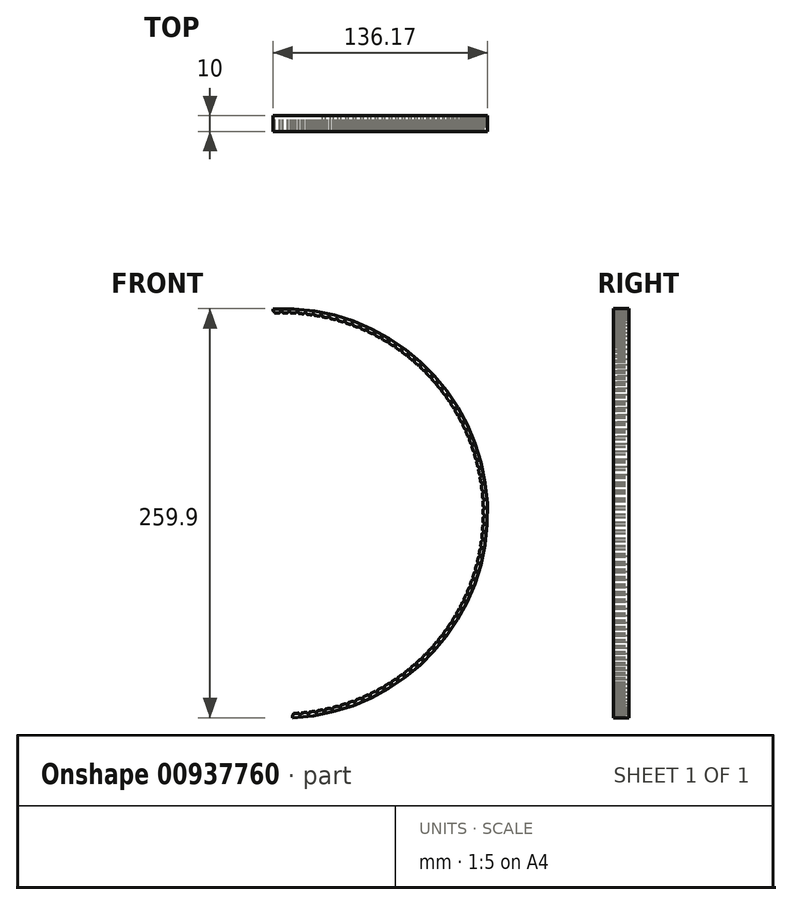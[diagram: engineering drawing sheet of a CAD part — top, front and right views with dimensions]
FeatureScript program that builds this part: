
annotation { "Feature Type Name" : "Feature", "Feature Type Description" : "" }
export const myFeature = defineFeature(function(context is Context, id is Id, definition is map)
    precondition{}
    {
        {
            var Q0;
            Q0=qCreatedBy(makeId("Front.planeOp"),FACE);
            var sketch = newSketch(context, id + "F0", { "sketchPlane" : qUnion([Q0])});
            skArc(sketch, "E0", {"start": v(-165.86, 72.13) * mm, "mid": v(-167.22, 72.1) * mm, "end": v(-168.6, 72.05) * mm});
            skArc(sketch, "E1", {"start": v(-157.54, -185.05) * mm, "mid": v(-33.83, -49.02) * mm, "end": v(-169.86, 74.7) * mm});
            skEllipticalArc(sketch, "E2.5.0.0", {});
            skArc(sketch, "E2.5.0.1", {"start": v(-169.02, 72.47) * mm, "mid": v(-168.84, 72.2) * mm, "end": v(-168.57, 72.04) * mm});
            skEllipticalArc(sketch, "E2.5.0.3", {});
            skEllipticalArc(sketch, "E3.1.0", {});
            skArc(sketch, "E3.1.1", {"start": v(-163.94, 72.58) * mm, "mid": v(-163.77, 72.31) * mm, "end": v(-163.5, 72.14) * mm});
            skEllipticalArc(sketch, "E3.2.0", {});
            skArc(sketch, "E3.2.1", {"start": v(-158.86, 72.49) * mm, "mid": v(-158.7, 72.21) * mm, "end": v(-158.45, 72.03) * mm});
            skEllipticalArc(sketch, "E3.3.0", {});
            skArc(sketch, "E3.3.1", {"start": v(-153.79, 72.2) * mm, "mid": v(-153.64, 71.91) * mm, "end": v(-153.4, 71.72) * mm});
            skEllipticalArc(sketch, "E3.4.0", {});
            skArc(sketch, "E3.4.1", {"start": v(-148.73, 71.7) * mm, "mid": v(-148.6, 71.41) * mm, "end": v(-148.36, 71.2) * mm});
            skEllipticalArc(sketch, "E3.5.0", {});
            skArc(sketch, "E3.5.1", {"start": v(-143.7, 71) * mm, "mid": v(-143.57, 70.71) * mm, "end": v(-143.34, 70.5) * mm});
            skEllipticalArc(sketch, "E3.6.0", {});
            skArc(sketch, "E3.6.1", {"start": v(-138.7, 70.1) * mm, "mid": v(-138.59, 69.81) * mm, "end": v(-138.36, 69.59) * mm});
            skEllipticalArc(sketch, "E3.7.0", {});
            skArc(sketch, "E3.7.1", {"start": v(-133.74, 69.01) * mm, "mid": v(-133.64, 68.71) * mm, "end": v(-133.42, 68.48) * mm});
            skEllipticalArc(sketch, "E3.8.0", {});
            skArc(sketch, "E3.8.1", {"start": v(-128.82, 67.72) * mm, "mid": v(-128.73, 67.42) * mm, "end": v(-128.53, 67.18) * mm});
            skEllipticalArc(sketch, "E3.9.0", {});
            skArc(sketch, "E3.9.1", {"start": v(-123.96, 66.24) * mm, "mid": v(-123.89, 65.93) * mm, "end": v(-123.7, 65.68) * mm});
            skEllipticalArc(sketch, "E3.10.0", {});
            skArc(sketch, "E3.10.1", {"start": v(-119.17, 64.56) * mm, "mid": v(-119.1, 64.25) * mm, "end": v(-118.92, 64) * mm});
            skEllipticalArc(sketch, "E3.11.0", {});
            skArc(sketch, "E3.11.1", {"start": v(-114.44, 62.7) * mm, "mid": v(-114.4, 62.39) * mm, "end": v(-114.22, 62.12) * mm});
            skEllipticalArc(sketch, "E3.12.0", {});
            skArc(sketch, "E3.12.1", {"start": v(-109.8, 60.64) * mm, "mid": v(-109.76, 60.33) * mm, "end": v(-109.6, 60.06) * mm});
            skEllipticalArc(sketch, "E3.13.0", {});
            skArc(sketch, "E3.13.1", {"start": v(-105.23, 58.4) * mm, "mid": v(-105.2, 58.1) * mm, "end": v(-105.06, 57.82) * mm});
            skEllipticalArc(sketch, "E3.14.0", {});
            skArc(sketch, "E3.14.1", {"start": v(-100.76, 56) * mm, "mid": v(-100.75, 55.68) * mm, "end": v(-100.6, 55.4) * mm});
            skEllipticalArc(sketch, "E3.15.0", {});
            skArc(sketch, "E3.15.1", {"start": v(-96.4, 53.4) * mm, "mid": v(-96.4, 53.09) * mm, "end": v(-96.26, 52.8) * mm});
            skEllipticalArc(sketch, "E3.16.0", {});
            skArc(sketch, "E3.16.1", {"start": v(-92.13, 50.64) * mm, "mid": v(-92.14, 50.33) * mm, "end": v(-92.02, 50.04) * mm});
            skEllipticalArc(sketch, "E3.17.0", {});
            skArc(sketch, "E3.17.1", {"start": v(-87.98, 47.71) * mm, "mid": v(-88, 47.4) * mm, "end": v(-87.9, 47.1) * mm});
            skEllipticalArc(sketch, "E3.18.0", {});
            skArc(sketch, "E3.18.1", {"start": v(-83.95, 44.62) * mm, "mid": v(-83.99, 44.3) * mm, "end": v(-83.9, 44) * mm});
            skEllipticalArc(sketch, "E3.19.0", {});
            skArc(sketch, "E3.19.1", {"start": v(-80.04, 41.37) * mm, "mid": v(-80.1, 41.06) * mm, "end": v(-80.01, 40.76) * mm});
            skEllipticalArc(sketch, "E3.20.0", {});
            skArc(sketch, "E3.20.1", {"start": v(-76.27, 37.97) * mm, "mid": v(-76.33, 37.66) * mm, "end": v(-76.26, 37.35) * mm});
            skEllipticalArc(sketch, "E3.21.0", {});
            skArc(sketch, "E3.21.1", {"start": v(-72.64, 34.42) * mm, "mid": v(-72.71, 34.11) * mm, "end": v(-72.65, 33.8) * mm});
            skEllipticalArc(sketch, "E3.22.0", {});
            skArc(sketch, "E3.22.1", {"start": v(-69.15, 30.73) * mm, "mid": v(-69.23, 30.42) * mm, "end": v(-69.19, 30.11) * mm});
            skEllipticalArc(sketch, "E3.23.0", {});
            skArc(sketch, "E3.23.1", {"start": v(-65.8, 26.9) * mm, "mid": v(-65.9, 26.6) * mm, "end": v(-65.87, 26.29) * mm});
            skEllipticalArc(sketch, "E3.24.0", {});
            skArc(sketch, "E3.24.1", {"start": v(-62.62, 22.94) * mm, "mid": v(-62.73, 22.65) * mm, "end": v(-62.71, 22.33) * mm});
            skEllipticalArc(sketch, "E3.25.0", {});
            skArc(sketch, "E3.25.1", {"start": v(-59.6, 18.86) * mm, "mid": v(-59.72, 18.57) * mm, "end": v(-59.7, 18.25) * mm});
            skEllipticalArc(sketch, "E3.26.0", {});
            skArc(sketch, "E3.26.1", {"start": v(-56.73, 14.66) * mm, "mid": v(-56.87, 14.38) * mm, "end": v(-56.87, 14.06) * mm});
            skEllipticalArc(sketch, "E3.27.0", {});
            skArc(sketch, "E3.27.1", {"start": v(-54.04, 10.35) * mm, "mid": v(-54.19, 10.07) * mm, "end": v(-54.2, 9.76) * mm});
            skEllipticalArc(sketch, "E3.28.0", {});
            skArc(sketch, "E3.28.1", {"start": v(-51.52, 5.94) * mm, "mid": v(-51.68, 5.67) * mm, "end": v(-51.7, 5.35) * mm});
            skEllipticalArc(sketch, "E3.29.0", {});
            skArc(sketch, "E3.29.1", {"start": v(-49.18, 1.43) * mm, "mid": v(-49.35, 1.17) * mm, "end": v(-49.4, 0.85) * mm});
            skEllipticalArc(sketch, "E3.30.0", {});
            skArc(sketch, "E3.30.1", {"start": v(-47.02, -3.16) * mm, "mid": v(-47.2, -3.42) * mm, "end": v(-47.25, -3.74) * mm});
            skEllipticalArc(sketch, "E3.31.0", {});
            skArc(sketch, "E3.31.1", {"start": v(-45.05, -7.84) * mm, "mid": v(-45.23, -8.1) * mm, "end": v(-45.3, -8.4) * mm});
            skEllipticalArc(sketch, "E3.32.0", {});
            skArc(sketch, "E3.32.1", {"start": v(-43.26, -12.6) * mm, "mid": v(-43.46, -12.85) * mm, "end": v(-43.53, -13.15) * mm});
            skEllipticalArc(sketch, "E3.33.0", {});
            skArc(sketch, "E3.33.1", {"start": v(-41.66, -17.42) * mm, "mid": v(-41.87, -17.66) * mm, "end": v(-41.96, -17.96) * mm});
            skEllipticalArc(sketch, "E3.34.0", {});
            skArc(sketch, "E3.34.1", {"start": v(-40.26, -22.3) * mm, "mid": v(-40.47, -22.53) * mm, "end": v(-40.58, -22.83) * mm});
            skEllipticalArc(sketch, "E3.35.0", {});
            skArc(sketch, "E3.35.1", {"start": v(-39.05, -27.24) * mm, "mid": v(-39.27, -27.46) * mm, "end": v(-39.39, -27.75) * mm});
            skEllipticalArc(sketch, "E3.36.0", {});
            skArc(sketch, "E3.36.1", {"start": v(-38.04, -32.22) * mm, "mid": v(-38.27, -32.43) * mm, "end": v(-38.4, -32.72) * mm});
            skEllipticalArc(sketch, "E3.37.0", {});
            skArc(sketch, "E3.37.1", {"start": v(-37.22, -37.23) * mm, "mid": v(-37.46, -37.43) * mm, "end": v(-37.6, -37.72) * mm});
            skEllipticalArc(sketch, "E3.38.0", {});
            skArc(sketch, "E3.38.1", {"start": v(-36.6, -42.27) * mm, "mid": v(-36.86, -42.47) * mm, "end": v(-37, -42.74) * mm});
            skEllipticalArc(sketch, "E3.39.0", {});
            skArc(sketch, "E3.39.1", {"start": v(-36.2, -47.34) * mm, "mid": v(-36.45, -47.52) * mm, "end": v(-36.61, -47.8) * mm});
            skEllipticalArc(sketch, "E3.40.0", {});
            skArc(sketch, "E3.40.1", {"start": v(-35.99, -52.41) * mm, "mid": v(-36.25, -52.59) * mm, "end": v(-36.42, -52.85) * mm});
            skEllipticalArc(sketch, "E3.41.0", {});
            skArc(sketch, "E3.41.1", {"start": v(-35.98, -57.5) * mm, "mid": v(-36.25, -57.65) * mm, "end": v(-36.43, -57.91) * mm});
            skEllipticalArc(sketch, "E3.42.0", {});
            skArc(sketch, "E3.42.1", {"start": v(-36.17, -62.57) * mm, "mid": v(-36.45, -62.72) * mm, "end": v(-36.64, -62.97) * mm});
            skEllipticalArc(sketch, "E3.43.0", {});
            skArc(sketch, "E3.43.1", {"start": v(-36.56, -67.63) * mm, "mid": v(-36.85, -67.77) * mm, "end": v(-37.05, -68.02) * mm});
            skEllipticalArc(sketch, "E3.44.0", {});
            skArc(sketch, "E3.44.1", {"start": v(-37.16, -72.68) * mm, "mid": v(-37.45, -72.8) * mm, "end": v(-37.66, -73.04) * mm});
            skEllipticalArc(sketch, "E3.45.0", {});
            skArc(sketch, "E3.45.1", {"start": v(-37.96, -77.7) * mm, "mid": v(-38.25, -77.81) * mm, "end": v(-38.47, -78.04) * mm});
            skEllipticalArc(sketch, "E3.46.0", {});
            skArc(sketch, "E3.46.1", {"start": v(-38.95, -82.68) * mm, "mid": v(-39.25, -82.78) * mm, "end": v(-39.48, -83) * mm});
            skEllipticalArc(sketch, "E3.47.0", {});
            skArc(sketch, "E3.47.1", {"start": v(-40.14, -87.62) * mm, "mid": v(-40.44, -87.71) * mm, "end": v(-40.68, -87.92) * mm});
            skEllipticalArc(sketch, "E3.48.0", {});
            skArc(sketch, "E3.48.1", {"start": v(-41.53, -92.5) * mm, "mid": v(-41.83, -92.59) * mm, "end": v(-42.08, -92.78) * mm});
            skEllipticalArc(sketch, "E3.49.0", {});
            skArc(sketch, "E3.49.1", {"start": v(-43.11, -97.33) * mm, "mid": v(-43.42, -97.4) * mm, "end": v(-43.67, -97.6) * mm});
            skEllipticalArc(sketch, "E3.50.0", {});
            skArc(sketch, "E3.50.1", {"start": v(-44.88, -102.1) * mm, "mid": v(-45.2, -102.15) * mm, "end": v(-45.45, -102.33) * mm});
            skEllipticalArc(sketch, "E3.51.0", {});
            skArc(sketch, "E3.51.1", {"start": v(-46.84, -106.78) * mm, "mid": v(-47.15, -106.83) * mm, "end": v(-47.42, -107) * mm});
            skEllipticalArc(sketch, "E3.52.0", {});
            skArc(sketch, "E3.52.1", {"start": v(-48.99, -111.39) * mm, "mid": v(-49.3, -111.42) * mm, "end": v(-49.57, -111.58) * mm});
            skEllipticalArc(sketch, "E3.53.0", {});
            skArc(sketch, "E3.53.1", {"start": v(-51.31, -115.9) * mm, "mid": v(-51.63, -115.92) * mm, "end": v(-51.9, -116.07) * mm});
            skEllipticalArc(sketch, "E3.54.0", {});
            skArc(sketch, "E3.54.1", {"start": v(-53.81, -120.32) * mm, "mid": v(-54.13, -120.33) * mm, "end": v(-54.41, -120.47) * mm});
            skEllipticalArc(sketch, "E3.55.0", {});
            skArc(sketch, "E3.55.1", {"start": v(-56.5, -124.64) * mm, "mid": v(-56.8, -124.64) * mm, "end": v(-57.1, -124.76) * mm});
            skEllipticalArc(sketch, "E3.56.0", {});
            skArc(sketch, "E3.56.1", {"start": v(-59.34, -128.85) * mm, "mid": v(-59.65, -128.83) * mm, "end": v(-59.95, -128.94) * mm});
            skEllipticalArc(sketch, "E3.57.0", {});
            skArc(sketch, "E3.57.1", {"start": v(-62.35, -132.94) * mm, "mid": v(-62.66, -132.91) * mm, "end": v(-62.96, -133.01) * mm});
            skEllipticalArc(sketch, "E3.58.0", {});
            skArc(sketch, "E3.58.1", {"start": v(-65.52, -136.9) * mm, "mid": v(-65.83, -136.87) * mm, "end": v(-66.13, -136.95) * mm});
            skEllipticalArc(sketch, "E3.59.0", {});
            skArc(sketch, "E3.59.1", {"start": v(-68.85, -140.75) * mm, "mid": v(-69.16, -140.7) * mm, "end": v(-69.46, -140.77) * mm});
            skEllipticalArc(sketch, "E3.60.0", {});
            skArc(sketch, "E3.60.1", {"start": v(-72.32, -144.45) * mm, "mid": v(-72.63, -144.38) * mm, "end": v(-72.94, -144.45) * mm});
            skEllipticalArc(sketch, "E3.61.0", {});
            skArc(sketch, "E3.61.1", {"start": v(-75.95, -148.02) * mm, "mid": v(-76.25, -147.94) * mm, "end": v(-76.56, -147.99) * mm});
            skEllipticalArc(sketch, "E3.62.0", {});
            skArc(sketch, "E3.62.1", {"start": v(-79.7, -151.43) * mm, "mid": v(-80, -151.34) * mm, "end": v(-80.32, -151.38) * mm});
            skEllipticalArc(sketch, "E3.63.0", {});
            skArc(sketch, "E3.63.1", {"start": v(-83.6, -154.7) * mm, "mid": v(-83.9, -154.6) * mm, "end": v(-84.21, -154.62) * mm});
            skEllipticalArc(sketch, "E3.64.0", {});
            skArc(sketch, "E3.64.1", {"start": v(-87.62, -157.8) * mm, "mid": v(-87.91, -157.69) * mm, "end": v(-88.23, -157.7) * mm});
            skEllipticalArc(sketch, "E3.65.0", {});
            skArc(sketch, "E3.65.1", {"start": v(-91.76, -160.75) * mm, "mid": v(-92.05, -160.62) * mm, "end": v(-92.36, -160.62) * mm});
            skEllipticalArc(sketch, "E3.66.0", {});
            skArc(sketch, "E3.66.1", {"start": v(-96.01, -163.52) * mm, "mid": v(-96.3, -163.38) * mm, "end": v(-96.61, -163.37) * mm});
            skEllipticalArc(sketch, "E3.67.0", {});
            skArc(sketch, "E3.67.1", {"start": v(-100.37, -166.13) * mm, "mid": v(-100.65, -165.98) * mm, "end": v(-100.97, -165.96) * mm});
            skEllipticalArc(sketch, "E3.68.0", {});
            skArc(sketch, "E3.68.1", {"start": v(-104.84, -168.56) * mm, "mid": v(-105.1, -168.4) * mm, "end": v(-105.42, -168.36) * mm});
            skEllipticalArc(sketch, "E3.69.0", {});
            skArc(sketch, "E3.69.1", {"start": v(-109.39, -170.8) * mm, "mid": v(-109.65, -170.64) * mm, "end": v(-109.96, -170.6) * mm});
            skEllipticalArc(sketch, "E3.70.0", {});
            skArc(sketch, "E3.70.1", {"start": v(-114.03, -172.88) * mm, "mid": v(-114.29, -172.7) * mm, "end": v(-114.6, -172.64) * mm});
            skEllipticalArc(sketch, "E3.71.0", {});
            skArc(sketch, "E3.71.1", {"start": v(-118.75, -174.76) * mm, "mid": v(-119, -174.57) * mm, "end": v(-119.3, -174.5) * mm});
            skEllipticalArc(sketch, "E3.72.0", {});
            skArc(sketch, "E3.72.1", {"start": v(-123.54, -176.45) * mm, "mid": v(-123.78, -176.25) * mm, "end": v(-124.08, -176.17) * mm});
            skEllipticalArc(sketch, "E3.73.0", {});
            skArc(sketch, "E3.73.1", {"start": v(-128.4, -177.95) * mm, "mid": v(-128.62, -177.74) * mm, "end": v(-128.92, -177.65) * mm});
            skEllipticalArc(sketch, "E3.74.0", {});
            skArc(sketch, "E3.74.1", {"start": v(-133.3, -179.26) * mm, "mid": v(-133.53, -179.04) * mm, "end": v(-133.82, -178.93) * mm});
            skEllipticalArc(sketch, "E3.75.0", {});
            skArc(sketch, "E3.75.1", {"start": v(-138.26, -180.37) * mm, "mid": v(-138.47, -180.14) * mm, "end": v(-138.76, -180.02) * mm});
            skEllipticalArc(sketch, "E3.76.0", {});
            skArc(sketch, "E3.76.1", {"start": v(-143.25, -181.29) * mm, "mid": v(-143.46, -181.05) * mm, "end": v(-143.75, -180.92) * mm});
            skEllipticalArc(sketch, "E3.77.0", {});
            skArc(sketch, "E3.77.1", {"start": v(-148.28, -182) * mm, "mid": v(-148.48, -181.75) * mm, "end": v(-148.76, -181.61) * mm});
            skEllipticalArc(sketch, "E3.78.0", {});
            skArc(sketch, "E3.78.1", {"start": v(-153.34, -182.51) * mm, "mid": v(-153.53, -182.26) * mm, "end": v(-153.8, -182.1) * mm});
            skLineSegment(sketch, "E3.anchor1", {"start": v(-163.71, -55.18) * mm, "end": v(-169.73, 72.2) * mm, "construction": true});
            skLineSegment(sketch, "E3.anchor2", {"start": v(-163.71, -55.18) * mm, "end": v(-157.7, -182.55) * mm, "construction": true});
            skArc(sketch, "E4.1.0", {"start": v(-165.86, 72.13) * mm, "mid": v(-165.56, 72.3) * mm, "end": v(-165.36, 72.57) * mm});
            skEllipticalArc(sketch, "E4.1.1", {});
            skArc(sketch, "E4.2.0", {"start": v(-160.8, 72.11) * mm, "mid": v(-160.49, 72.27) * mm, "end": v(-160.28, 72.54) * mm});
            skEllipticalArc(sketch, "E4.2.1", {});
            skArc(sketch, "E4.3.0", {"start": v(-155.74, 71.9) * mm, "mid": v(-155.42, 72.04) * mm, "end": v(-155.2, 72.3) * mm});
            skEllipticalArc(sketch, "E4.3.1", {});
            skArc(sketch, "E4.4.0", {"start": v(-150.69, 71.48) * mm, "mid": v(-150.37, 71.6) * mm, "end": v(-150.15, 71.86) * mm});
            skEllipticalArc(sketch, "E4.4.1", {});
            skArc(sketch, "E4.5.0", {"start": v(-145.66, 70.86) * mm, "mid": v(-145.34, 70.98) * mm, "end": v(-145.1, 71.22) * mm});
            skEllipticalArc(sketch, "E4.5.1", {});
            skArc(sketch, "E4.6.0", {"start": v(-140.67, 70.04) * mm, "mid": v(-140.34, 70.15) * mm, "end": v(-140.1, 70.38) * mm});
            skEllipticalArc(sketch, "E4.6.1", {});
            skArc(sketch, "E4.7.0", {"start": v(-135.7, 69.03) * mm, "mid": v(-135.38, 69.12) * mm, "end": v(-135.12, 69.34) * mm});
            skEllipticalArc(sketch, "E4.7.1", {});
            skArc(sketch, "E4.8.0", {"start": v(-130.8, 67.82) * mm, "mid": v(-130.46, 67.9) * mm, "end": v(-130.2, 68.1) * mm});
            skEllipticalArc(sketch, "E4.8.1", {});
            skArc(sketch, "E4.9.0", {"start": v(-125.93, 66.41) * mm, "mid": v(-125.6, 66.47) * mm, "end": v(-125.32, 66.68) * mm});
            skEllipticalArc(sketch, "E4.9.1", {});
            skArc(sketch, "E4.10.0", {"start": v(-121.12, 64.81) * mm, "mid": v(-120.79, 64.86) * mm, "end": v(-120.5, 65.06) * mm});
            skEllipticalArc(sketch, "E4.10.1", {});
            skArc(sketch, "E4.11.0", {"start": v(-116.39, 63.02) * mm, "mid": v(-116.05, 63.06) * mm, "end": v(-115.76, 63.24) * mm});
            skEllipticalArc(sketch, "E4.11.1", {});
            skArc(sketch, "E4.12.0", {"start": v(-111.73, 61.05) * mm, "mid": v(-111.38, 61.07) * mm, "end": v(-111.09, 61.24) * mm});
            skEllipticalArc(sketch, "E4.12.1", {});
            skArc(sketch, "E4.13.0", {"start": v(-107.15, 58.9) * mm, "mid": v(-106.8, 58.9) * mm, "end": v(-106.5, 59.06) * mm});
            skEllipticalArc(sketch, "E4.13.1", {});
            skArc(sketch, "E4.14.0", {"start": v(-102.66, 56.55) * mm, "mid": v(-102.31, 56.55) * mm, "end": v(-102, 56.7) * mm});
            skEllipticalArc(sketch, "E4.14.1", {});
            skArc(sketch, "E4.15.0", {"start": v(-98.26, 54.04) * mm, "mid": v(-97.92, 54.02) * mm, "end": v(-97.6, 54.15) * mm});
            skEllipticalArc(sketch, "E4.15.1", {});
            skArc(sketch, "E4.16.0", {"start": v(-93.97, 51.35) * mm, "mid": v(-93.63, 51.32) * mm, "end": v(-93.31, 51.44) * mm});
            skEllipticalArc(sketch, "E4.16.1", {});
            skArc(sketch, "E4.17.0", {"start": v(-89.8, 48.5) * mm, "mid": v(-89.45, 48.45) * mm, "end": v(-89.13, 48.56) * mm});
            skEllipticalArc(sketch, "E4.17.1", {});
            skArc(sketch, "E4.18.0", {"start": v(-85.73, 45.47) * mm, "mid": v(-85.4, 45.41) * mm, "end": v(-85.06, 45.5) * mm});
            skEllipticalArc(sketch, "E4.18.1", {});
            skArc(sketch, "E4.19.0", {"start": v(-81.79, 42.29) * mm, "mid": v(-81.45, 42.22) * mm, "end": v(-81.12, 42.3) * mm});
            skEllipticalArc(sketch, "E4.19.1", {});
            skArc(sketch, "E4.20.0", {"start": v(-77.98, 38.96) * mm, "mid": v(-77.65, 38.87) * mm, "end": v(-77.31, 38.94) * mm});
            skEllipticalArc(sketch, "E4.20.1", {});
            skArc(sketch, "E4.21.0", {"start": v(-74.3, 35.47) * mm, "mid": v(-73.98, 35.37) * mm, "end": v(-73.64, 35.43) * mm});
            skEllipticalArc(sketch, "E4.21.1", {});
            skArc(sketch, "E4.22.0", {"start": v(-70.77, 31.85) * mm, "mid": v(-70.45, 31.74) * mm, "end": v(-70.1, 31.78) * mm});
            skEllipticalArc(sketch, "E4.22.1", {});
            skArc(sketch, "E4.23.0", {"start": v(-67.38, 28.08) * mm, "mid": v(-67.07, 27.96) * mm, "end": v(-66.73, 27.99) * mm});
            skEllipticalArc(sketch, "E4.23.1", {});
            skArc(sketch, "E4.24.0", {"start": v(-64.15, 24.19) * mm, "mid": v(-63.84, 24.05) * mm, "end": v(-63.5, 24.07) * mm});
            skEllipticalArc(sketch, "E4.24.1", {});
            skArc(sketch, "E4.25.0", {"start": v(-61.07, 20.17) * mm, "mid": v(-60.77, 20.02) * mm, "end": v(-60.42, 20.02) * mm});
            skEllipticalArc(sketch, "E4.25.1", {});
            skArc(sketch, "E4.26.0", {"start": v(-58.16, 16.03) * mm, "mid": v(-57.86, 15.87) * mm, "end": v(-57.52, 15.85) * mm});
            skEllipticalArc(sketch, "E4.26.1", {});
            skArc(sketch, "E4.27.0", {"start": v(-55.41, 11.77) * mm, "mid": v(-55.12, 11.6) * mm, "end": v(-54.78, 11.58) * mm});
            skEllipticalArc(sketch, "E4.27.1", {});
            skArc(sketch, "E4.28.0", {"start": v(-52.84, 7.41) * mm, "mid": v(-52.55, 7.23) * mm, "end": v(-52.2, 7.2) * mm});
            skEllipticalArc(sketch, "E4.28.1", {});
            skArc(sketch, "E4.29.0", {"start": v(-50.44, 2.96) * mm, "mid": v(-50.16, 2.76) * mm, "end": v(-49.82, 2.71) * mm});
            skEllipticalArc(sketch, "E4.29.1", {});
            skArc(sketch, "E4.30.0", {"start": v(-48.21, -1.6) * mm, "mid": v(-47.94, -1.8) * mm, "end": v(-47.6, -1.86) * mm});
            skEllipticalArc(sketch, "E4.30.1", {});
            skArc(sketch, "E4.31.0", {"start": v(-46.17, -6.23) * mm, "mid": v(-45.91, -6.44) * mm, "end": v(-45.58, -6.52) * mm});
            skEllipticalArc(sketch, "E4.31.1", {});
            skArc(sketch, "E4.32.0", {"start": v(-44.32, -10.94) * mm, "mid": v(-44.07, -11.17) * mm, "end": v(-43.74, -11.26) * mm});
            skEllipticalArc(sketch, "E4.32.1", {});
            skArc(sketch, "E4.33.0", {"start": v(-42.66, -15.72) * mm, "mid": v(-42.41, -15.96) * mm, "end": v(-42.09, -16.06) * mm});
            skEllipticalArc(sketch, "E4.33.1", {});
            skArc(sketch, "E4.34.0", {"start": v(-41.18, -20.56) * mm, "mid": v(-40.95, -20.81) * mm, "end": v(-40.63, -20.93) * mm});
            skEllipticalArc(sketch, "E4.34.1", {});
            skArc(sketch, "E4.35.0", {"start": v(-39.9, -25.46) * mm, "mid": v(-39.68, -25.72) * mm, "end": v(-39.36, -25.85) * mm});
            skEllipticalArc(sketch, "E4.35.1", {});
            skArc(sketch, "E4.36.0", {"start": v(-38.82, -30.4) * mm, "mid": v(-38.6, -30.67) * mm, "end": v(-38.3, -30.81) * mm});
            skEllipticalArc(sketch, "E4.36.1", {});
            skArc(sketch, "E4.37.0", {"start": v(-37.94, -35.4) * mm, "mid": v(-37.73, -35.67) * mm, "end": v(-37.43, -35.82) * mm});
            skEllipticalArc(sketch, "E4.37.1", {});
            skArc(sketch, "E4.38.0", {"start": v(-37.25, -40.4) * mm, "mid": v(-37.05, -40.7) * mm, "end": v(-36.76, -40.86) * mm});
            skEllipticalArc(sketch, "E4.38.1", {});
            skArc(sketch, "E4.39.0", {"start": v(-36.76, -45.45) * mm, "mid": v(-36.58, -45.74) * mm, "end": v(-36.29, -45.92) * mm});
            skEllipticalArc(sketch, "E4.39.1", {});
            skArc(sketch, "E4.40.0", {"start": v(-36.47, -50.5) * mm, "mid": v(-36.3, -50.8) * mm, "end": v(-36.02, -50.99) * mm});
            skEllipticalArc(sketch, "E4.40.1", {});
            skArc(sketch, "E4.41.0", {"start": v(-36.39, -55.56) * mm, "mid": v(-36.23, -55.87) * mm, "end": v(-35.95, -56.07) * mm});
            skEllipticalArc(sketch, "E4.41.1", {});
            skArc(sketch, "E4.42.0", {"start": v(-36.5, -60.63) * mm, "mid": v(-36.36, -60.94) * mm, "end": v(-36.09, -61.15) * mm});
            skEllipticalArc(sketch, "E4.42.1", {});
            skArc(sketch, "E4.43.0", {"start": v(-36.82, -65.68) * mm, "mid": v(-36.69, -66) * mm, "end": v(-36.43, -66.22) * mm});
            skEllipticalArc(sketch, "E4.43.1", {});
            skArc(sketch, "E4.44.0", {"start": v(-37.34, -70.72) * mm, "mid": v(-37.22, -71.04) * mm, "end": v(-36.97, -71.27) * mm});
            skEllipticalArc(sketch, "E4.44.1", {});
            skArc(sketch, "E4.45.0", {"start": v(-38.06, -75.73) * mm, "mid": v(-37.95, -76.05) * mm, "end": v(-37.7, -76.3) * mm});
            skEllipticalArc(sketch, "E4.45.1", {});
            skArc(sketch, "E4.46.0", {"start": v(-38.97, -80.7) * mm, "mid": v(-38.88, -81.04) * mm, "end": v(-38.65, -81.29) * mm});
            skEllipticalArc(sketch, "E4.46.1", {});
            skArc(sketch, "E4.47.0", {"start": v(-40.09, -85.65) * mm, "mid": v(-40, -85.98) * mm, "end": v(-39.78, -86.24) * mm});
            skEllipticalArc(sketch, "E4.47.1", {});
            skArc(sketch, "E4.48.0", {"start": v(-41.4, -90.54) * mm, "mid": v(-41.33, -90.87) * mm, "end": v(-41.12, -91.14) * mm});
            skEllipticalArc(sketch, "E4.48.1", {});
            skArc(sketch, "E4.49.0", {"start": v(-42.9, -95.37) * mm, "mid": v(-42.84, -95.7) * mm, "end": v(-42.64, -95.99) * mm});
            skEllipticalArc(sketch, "E4.49.1", {});
            skArc(sketch, "E4.50.0", {"start": v(-44.6, -100.14) * mm, "mid": v(-44.55, -100.48) * mm, "end": v(-44.36, -100.77) * mm});
            skEllipticalArc(sketch, "E4.50.1", {});
            skArc(sketch, "E4.51.0", {"start": v(-46.47, -104.84) * mm, "mid": v(-46.45, -105.18) * mm, "end": v(-46.27, -105.48) * mm});
            skEllipticalArc(sketch, "E4.51.1", {});
            skArc(sketch, "E4.52.0", {"start": v(-48.54, -109.46) * mm, "mid": v(-48.53, -109.8) * mm, "end": v(-48.36, -110.1) * mm});
            skEllipticalArc(sketch, "E4.52.1", {});
            skArc(sketch, "E4.53.0", {"start": v(-50.8, -114) * mm, "mid": v(-50.79, -114.34) * mm, "end": v(-50.64, -114.65) * mm});
            skEllipticalArc(sketch, "E4.53.1", {});
            skArc(sketch, "E4.54.0", {"start": v(-53.22, -118.44) * mm, "mid": v(-53.23, -118.79) * mm, "end": v(-53.09, -119.1) * mm});
            skEllipticalArc(sketch, "E4.54.1", {});
            skArc(sketch, "E4.55.0", {"start": v(-55.82, -122.79) * mm, "mid": v(-55.85, -123.13) * mm, "end": v(-55.72, -123.44) * mm});
            skEllipticalArc(sketch, "E4.55.1", {});
            skArc(sketch, "E4.56.0", {"start": v(-58.6, -127.02) * mm, "mid": v(-58.63, -127.36) * mm, "end": v(-58.52, -127.68) * mm});
            skEllipticalArc(sketch, "E4.56.1", {});
            skArc(sketch, "E4.57.0", {"start": v(-61.53, -131.14) * mm, "mid": v(-61.59, -131.48) * mm, "end": v(-61.48, -131.8) * mm});
            skEllipticalArc(sketch, "E4.57.1", {});
            skArc(sketch, "E4.58.0", {"start": v(-64.64, -135.15) * mm, "mid": v(-64.7, -135.48) * mm, "end": v(-64.61, -135.81) * mm});
            skEllipticalArc(sketch, "E4.58.1", {});
            skArc(sketch, "E4.59.0", {"start": v(-67.9, -139.02) * mm, "mid": v(-67.97, -139.36) * mm, "end": v(-67.9, -139.69) * mm});
            skEllipticalArc(sketch, "E4.59.1", {});
            skArc(sketch, "E4.60.0", {"start": v(-71.3, -142.77) * mm, "mid": v(-71.4, -143.1) * mm, "end": v(-71.33, -143.43) * mm});
            skEllipticalArc(sketch, "E4.60.1", {});
            skArc(sketch, "E4.61.0", {"start": v(-74.86, -146.37) * mm, "mid": v(-74.96, -146.7) * mm, "end": v(-74.91, -147.03) * mm});
            skEllipticalArc(sketch, "E4.61.1", {});
            skArc(sketch, "E4.62.0", {"start": v(-78.55, -149.83) * mm, "mid": v(-78.67, -150.15) * mm, "end": v(-78.63, -150.5) * mm});
            skEllipticalArc(sketch, "E4.62.1", {});
            skArc(sketch, "E4.63.0", {"start": v(-82.38, -153.14) * mm, "mid": v(-82.51, -153.46) * mm, "end": v(-82.5, -153.8) * mm});
            skEllipticalArc(sketch, "E4.63.1", {});
            skArc(sketch, "E4.64.0", {"start": v(-86.34, -156.3) * mm, "mid": v(-86.49, -156.6) * mm, "end": v(-86.48, -156.95) * mm});
            skEllipticalArc(sketch, "E4.64.1", {});
            skArc(sketch, "E4.65.0", {"start": v(-90.42, -159.3) * mm, "mid": v(-90.58, -159.6) * mm, "end": v(-90.58, -159.94) * mm});
            skEllipticalArc(sketch, "E4.65.1", {});
            skArc(sketch, "E4.66.0", {"start": v(-94.62, -162.12) * mm, "mid": v(-94.79, -162.42) * mm, "end": v(-94.8, -162.76) * mm});
            skEllipticalArc(sketch, "E4.66.1", {});
            skArc(sketch, "E4.67.0", {"start": v(-98.93, -164.79) * mm, "mid": v(-99.1, -165.08) * mm, "end": v(-99.14, -165.42) * mm});
            skEllipticalArc(sketch, "E4.67.1", {});
            skArc(sketch, "E4.68.0", {"start": v(-103.34, -167.28) * mm, "mid": v(-103.53, -167.56) * mm, "end": v(-103.57, -167.9) * mm});
            skEllipticalArc(sketch, "E4.68.1", {});
            skArc(sketch, "E4.69.0", {"start": v(-107.84, -169.59) * mm, "mid": v(-108.04, -169.86) * mm, "end": v(-108.1, -170.2) * mm});
            skEllipticalArc(sketch, "E4.69.1", {});
            skArc(sketch, "E4.70.0", {"start": v(-112.43, -171.72) * mm, "mid": v(-112.65, -171.99) * mm, "end": v(-112.72, -172.32) * mm});
            skEllipticalArc(sketch, "E4.70.1", {});
            skArc(sketch, "E4.71.0", {"start": v(-117.1, -173.66) * mm, "mid": v(-117.33, -173.92) * mm, "end": v(-117.41, -174.26) * mm});
            skEllipticalArc(sketch, "E4.71.1", {});
            skArc(sketch, "E4.72.0", {"start": v(-121.86, -175.42) * mm, "mid": v(-122.09, -175.67) * mm, "end": v(-122.19, -176) * mm});
            skEllipticalArc(sketch, "E4.72.1", {});
            skArc(sketch, "E4.73.0", {"start": v(-126.67, -177) * mm, "mid": v(-126.91, -177.23) * mm, "end": v(-127.02, -177.56) * mm});
            skEllipticalArc(sketch, "E4.73.1", {});
            skArc(sketch, "E4.74.0", {"start": v(-131.54, -178.37) * mm, "mid": v(-131.8, -178.6) * mm, "end": v(-131.92, -178.92) * mm});
            skEllipticalArc(sketch, "E4.74.1", {});
            skArc(sketch, "E4.75.0", {"start": v(-136.46, -179.55) * mm, "mid": v(-136.73, -179.77) * mm, "end": v(-136.86, -180.09) * mm});
            skEllipticalArc(sketch, "E4.75.1", {});
            skArc(sketch, "E4.76.0", {"start": v(-141.43, -180.54) * mm, "mid": v(-141.7, -180.75) * mm, "end": v(-141.85, -181.05) * mm});
            skEllipticalArc(sketch, "E4.76.1", {});
            skArc(sketch, "E4.77.0", {"start": v(-146.43, -181.32) * mm, "mid": v(-146.7, -181.52) * mm, "end": v(-146.87, -181.82) * mm});
            skEllipticalArc(sketch, "E4.77.1", {});
            skArc(sketch, "E4.78.0", {"start": v(-151.46, -181.91) * mm, "mid": v(-151.75, -182.1) * mm, "end": v(-151.92, -182.4) * mm});
            skEllipticalArc(sketch, "E4.78.1", {});
            skArc(sketch, "E4.79.0", {"start": v(-156.5, -182.3) * mm, "mid": v(-156.8, -182.47) * mm, "end": v(-156.99, -182.76) * mm});
            skEllipticalArc(sketch, "E4.79.1", {});
            skLineSegment(sketch, "E4.anchor1", {"start": v(-163.71, -55.18) * mm, "end": v(-170.92, 71.94) * mm, "construction": true});
            skLineSegment(sketch, "E4.anchor2", {"start": v(-163.71, -55.18) * mm, "end": v(-156.5, -182.3) * mm, "construction": true});
            skLineSegment(sketch, "E5", {"start": v(-169.72, 72) * mm, "end": v(-169.78, 73.2) * mm});
            skLineSegment(sketch, "E6", {"start": v(-169.72, 72) * mm, "end": v(-169.72, 71.88) * mm});
            skLineSegment(sketch, "E7", {"start": v(-169.77, 73.2) * mm, "end": v(-169.86, 74.7) * mm});
            skArc(sketch, "E8.trimOffspring", {"start": v(-156.5, -182.3) * mm, "mid": v(-155.14, -182.21) * mm, "end": v(-153.78, -182.11) * mm});
            skLineSegment(sketch, "E9", {"start": v(-157.7, -182.36) * mm, "end": v(-157.54, -185.05) * mm});
            skArc(sketch, "E10.trimOffspring", {"start": v(-151.46, -181.91) * mm, "mid": v(-150.1, -181.77) * mm, "end": v(-148.74, -181.62) * mm});
            skArc(sketch, "E11.trimOffspring", {"start": v(-146.43, -181.32) * mm, "mid": v(-145.08, -181.13) * mm, "end": v(-143.72, -180.92) * mm});
            skArc(sketch, "E12.trimOffspring", {"start": v(-141.43, -180.54) * mm, "mid": v(-140.08, -180.29) * mm, "end": v(-138.74, -180.03) * mm});
            skArc(sketch, "E13.trimOffspring", {"start": v(-136.46, -179.55) * mm, "mid": v(-135.13, -179.25) * mm, "end": v(-133.8, -178.94) * mm});
            skArc(sketch, "E14.trimOffspring", {"start": v(-131.54, -178.37) * mm, "mid": v(-130.22, -178.02) * mm, "end": v(-128.9, -177.65) * mm});
            skArc(sketch, "E15.trimOffspring", {"start": v(-126.67, -177) * mm, "mid": v(-125.36, -176.59) * mm, "end": v(-124.06, -176.17) * mm});
            skArc(sketch, "E16.trimOffspring", {"start": v(-121.86, -175.42) * mm, "mid": v(-120.57, -174.97) * mm, "end": v(-119.28, -174.5) * mm});
            skArc(sketch, "E17.trimOffspring", {"start": v(-117.1, -173.66) * mm, "mid": v(-115.84, -173.16) * mm, "end": v(-114.57, -172.64) * mm});
            skArc(sketch, "E18.trimOffspring", {"start": v(-112.43, -171.72) * mm, "mid": v(-111.18, -171.16) * mm, "end": v(-109.94, -170.59) * mm});
            skArc(sketch, "E19.trimOffspring", {"start": v(-107.84, -169.59) * mm, "mid": v(-106.61, -168.98) * mm, "end": v(-105.4, -168.36) * mm});
            skArc(sketch, "E20.trimOffspring", {"start": v(-103.34, -167.28) * mm, "mid": v(-102.14, -166.62) * mm, "end": v(-100.94, -165.95) * mm});
            skArc(sketch, "E21.trimOffspring", {"start": v(-98.93, -164.79) * mm, "mid": v(-97.75, -164.08) * mm, "end": v(-96.59, -163.37) * mm});
            skArc(sketch, "E22.trimOffspring", {"start": v(-94.62, -162.12) * mm, "mid": v(-93.48, -161.38) * mm, "end": v(-92.34, -160.62) * mm});
            skArc(sketch, "E23.trimOffspring", {"start": v(-90.42, -159.3) * mm, "mid": v(-89.3, -158.5) * mm, "end": v(-88.2, -157.7) * mm});
            skArc(sketch, "E24.trimOffspring", {"start": v(-86.34, -156.3) * mm, "mid": v(-85.26, -155.46) * mm, "end": v(-84.19, -154.61) * mm});
            skArc(sketch, "E25.trimOffspring", {"start": v(-82.38, -153.14) * mm, "mid": v(-81.34, -152.26) * mm, "end": v(-80.3, -151.37) * mm});
            skArc(sketch, "E26.trimOffspring", {"start": v(-78.55, -149.83) * mm, "mid": v(-77.54, -148.9) * mm, "end": v(-76.54, -147.98) * mm});
            skArc(sketch, "E27.trimOffspring", {"start": v(-74.86, -146.37) * mm, "mid": v(-73.88, -145.41) * mm, "end": v(-72.92, -144.44) * mm});
            skArc(sketch, "E28.trimOffspring", {"start": v(-71.3, -142.77) * mm, "mid": v(-70.37, -141.77) * mm, "end": v(-69.44, -140.76) * mm});
            skArc(sketch, "E29.trimOffspring", {"start": v(-67.9, -139.02) * mm, "mid": v(-67, -137.99) * mm, "end": v(-66.11, -136.94) * mm});
            skArc(sketch, "E30.trimOffspring", {"start": v(-64.64, -135.15) * mm, "mid": v(-63.78, -134.08) * mm, "end": v(-62.94, -133) * mm});
            skArc(sketch, "E31.trimOffspring", {"start": v(-61.53, -131.14) * mm, "mid": v(-60.72, -130.04) * mm, "end": v(-59.93, -128.93) * mm});
            skArc(sketch, "E32.trimOffspring", {"start": v(-58.6, -127.02) * mm, "mid": v(-57.83, -125.89) * mm, "end": v(-57.08, -124.75) * mm});
            skArc(sketch, "E33.trimOffspring", {"start": v(-55.82, -122.79) * mm, "mid": v(-55.1, -121.62) * mm, "end": v(-54.4, -120.45) * mm});
            skArc(sketch, "E34.trimOffspring", {"start": v(-53.22, -118.44) * mm, "mid": v(-52.55, -117.25) * mm, "end": v(-51.89, -116.05) * mm});
            skArc(sketch, "E35.trimOffspring", {"start": v(-50.8, -114) * mm, "mid": v(-50.17, -112.78) * mm, "end": v(-49.55, -111.56) * mm});
            skArc(sketch, "E36.trimOffspring", {"start": v(-48.54, -109.46) * mm, "mid": v(-47.97, -108.22) * mm, "end": v(-47.4, -106.98) * mm});
            skArc(sketch, "E37.trimOffspring", {"start": v(-46.47, -104.84) * mm, "mid": v(-45.95, -103.58) * mm, "end": v(-45.43, -102.31) * mm});
            skArc(sketch, "E38.trimOffspring", {"start": v(-44.6, -100.14) * mm, "mid": v(-44.12, -98.86) * mm, "end": v(-43.65, -97.57) * mm});
            skArc(sketch, "E39.trimOffspring", {"start": v(-42.9, -95.37) * mm, "mid": v(-42.47, -94.07) * mm, "end": v(-42.06, -92.77) * mm});
            skArc(sketch, "E40.trimOffspring", {"start": v(-41.4, -90.54) * mm, "mid": v(-41.02, -89.22) * mm, "end": v(-40.67, -87.9) * mm});
            skArc(sketch, "E41.trimOffspring", {"start": v(-40.09, -85.65) * mm, "mid": v(-39.77, -84.32) * mm, "end": v(-39.46, -82.98) * mm});
            skArc(sketch, "E42.trimOffspring", {"start": v(-38.97, -80.7) * mm, "mid": v(-38.7, -79.36) * mm, "end": v(-38.45, -78.02) * mm});
            skArc(sketch, "E43.trimOffspring", {"start": v(-38.06, -75.73) * mm, "mid": v(-37.84, -74.38) * mm, "end": v(-37.65, -73.02) * mm});
            skArc(sketch, "E44.trimOffspring", {"start": v(-37.34, -70.72) * mm, "mid": v(-37.18, -69.36) * mm, "end": v(-37.04, -68) * mm});
            skArc(sketch, "E45.trimOffspring", {"start": v(-36.82, -65.68) * mm, "mid": v(-36.72, -64.32) * mm, "end": v(-36.63, -62.95) * mm});
            skArc(sketch, "E46.trimOffspring", {"start": v(-36.5, -60.63) * mm, "mid": v(-36.45, -59.26) * mm, "end": v(-36.42, -57.9) * mm});
            skArc(sketch, "E47.trimOffspring", {"start": v(-36.39, -55.56) * mm, "mid": v(-36.4, -54.2) * mm, "end": v(-36.41, -52.83) * mm});
            skArc(sketch, "E48.trimOffspring", {"start": v(-36.47, -50.5) * mm, "mid": v(-36.53, -49.14) * mm, "end": v(-36.6, -47.77) * mm});
            skArc(sketch, "E49.trimOffspring", {"start": v(-36.76, -45.45) * mm, "mid": v(-36.87, -44.08) * mm, "end": v(-37, -42.72) * mm});
            skArc(sketch, "E50.trimOffspring", {"start": v(-37.25, -40.4) * mm, "mid": v(-37.41, -39.05) * mm, "end": v(-37.6, -37.7) * mm});
            skArc(sketch, "E51.trimOffspring", {"start": v(-37.94, -35.4) * mm, "mid": v(-38.16, -34.04) * mm, "end": v(-38.39, -32.7) * mm});
            skArc(sketch, "E52.trimOffspring", {"start": v(-38.82, -30.4) * mm, "mid": v(-39.1, -29.07) * mm, "end": v(-39.38, -27.73) * mm});
            skArc(sketch, "E53.trimOffspring", {"start": v(-39.9, -25.46) * mm, "mid": v(-40.23, -24.13) * mm, "end": v(-40.57, -22.8) * mm});
            skArc(sketch, "E54.trimOffspring", {"start": v(-41.18, -20.56) * mm, "mid": v(-41.56, -19.25) * mm, "end": v(-41.96, -17.94) * mm});
            skArc(sketch, "E55.trimOffspring", {"start": v(-42.66, -15.72) * mm, "mid": v(-43.09, -14.42) * mm, "end": v(-43.53, -13.13) * mm});
            skArc(sketch, "E56.trimOffspring", {"start": v(-44.32, -10.94) * mm, "mid": v(-44.8, -9.66) * mm, "end": v(-45.3, -8.38) * mm});
            skArc(sketch, "E57.trimOffspring", {"start": v(-46.17, -6.23) * mm, "mid": v(-46.7, -4.97) * mm, "end": v(-47.25, -3.71) * mm});
            skArc(sketch, "E58.trimOffspring", {"start": v(-48.21, -1.6) * mm, "mid": v(-48.8, -0.35) * mm, "end": v(-49.4, 0.88) * mm});
            skArc(sketch, "E59.trimOffspring", {"start": v(-50.44, 2.96) * mm, "mid": v(-51.07, 4.17) * mm, "end": v(-51.71, 5.38) * mm});
            skArc(sketch, "E60.trimOffspring", {"start": v(-52.84, 7.41) * mm, "mid": v(-53.52, 8.6) * mm, "end": v(-54.2, 9.78) * mm});
            skArc(sketch, "E61.trimOffspring", {"start": v(-55.41, 11.77) * mm, "mid": v(-56.14, 12.93) * mm, "end": v(-56.88, 14.09) * mm});
            skArc(sketch, "E62.trimOffspring", {"start": v(-58.16, 16.03) * mm, "mid": v(-58.93, 17.16) * mm, "end": v(-59.71, 18.28) * mm});
            skArc(sketch, "E63.trimOffspring", {"start": v(-61.07, 20.17) * mm, "mid": v(-61.89, 21.27) * mm, "end": v(-62.72, 22.35) * mm});
            skArc(sketch, "E64.trimOffspring", {"start": v(-64.15, 24.19) * mm, "mid": v(-65, 25.25) * mm, "end": v(-65.88, 26.3) * mm});
            skArc(sketch, "E65.trimOffspring", {"start": v(-67.38, 28.08) * mm, "mid": v(-68.29, 29.11) * mm, "end": v(-69.2, 30.13) * mm});
            skArc(sketch, "E66.trimOffspring", {"start": v(-70.77, 31.85) * mm, "mid": v(-71.71, 32.84) * mm, "end": v(-72.66, 33.82) * mm});
            skArc(sketch, "E67.trimOffspring", {"start": v(-74.3, 35.47) * mm, "mid": v(-75.28, 36.43) * mm, "end": v(-76.27, 37.37) * mm});
            skArc(sketch, "E68.trimOffspring", {"start": v(-77.98, 38.96) * mm, "mid": v(-79, 39.87) * mm, "end": v(-80.02, 40.78) * mm});
            skArc(sketch, "E69.trimOffspring", {"start": v(-81.79, 42.29) * mm, "mid": v(-82.84, 43.16) * mm, "end": v(-83.9, 44.03) * mm});
            skArc(sketch, "E70.trimOffspring", {"start": v(-85.73, 45.47) * mm, "mid": v(-86.82, 46.3) * mm, "end": v(-87.91, 47.12) * mm});
            skArc(sketch, "E71.trimOffspring", {"start": v(-89.8, 48.5) * mm, "mid": v(-90.91, 49.28) * mm, "end": v(-92.04, 50.06) * mm});
            skArc(sketch, "E72.trimOffspring", {"start": v(-93.97, 51.35) * mm, "mid": v(-95.12, 52.1) * mm, "end": v(-96.28, 52.82) * mm});
            skArc(sketch, "E73.trimOffspring", {"start": v(-98.26, 54.04) * mm, "mid": v(-99.44, 54.73) * mm, "end": v(-100.62, 55.42) * mm});
            skArc(sketch, "E74.trimOffspring", {"start": v(-102.66, 56.55) * mm, "mid": v(-103.86, 57.2) * mm, "end": v(-105.07, 57.84) * mm});
            skArc(sketch, "E75.trimOffspring", {"start": v(-107.15, 58.9) * mm, "mid": v(-108.38, 59.5) * mm, "end": v(-109.61, 60.08) * mm});
            skArc(sketch, "E76.trimOffspring", {"start": v(-111.73, 61.05) * mm, "mid": v(-112.98, 61.6) * mm, "end": v(-114.24, 62.14) * mm});
            skArc(sketch, "E77.trimOffspring", {"start": v(-116.39, 63.02) * mm, "mid": v(-117.66, 63.53) * mm, "end": v(-118.94, 64.01) * mm});
            skArc(sketch, "E78.trimOffspring", {"start": v(-121.12, 64.81) * mm, "mid": v(-122.42, 65.26) * mm, "end": v(-123.71, 65.7) * mm});
            skArc(sketch, "E79.trimOffspring", {"start": v(-125.93, 66.41) * mm, "mid": v(-127.24, 66.8) * mm, "end": v(-128.55, 67.2) * mm});
            skArc(sketch, "E80.trimOffspring", {"start": v(-130.8, 67.82) * mm, "mid": v(-132.12, 68.16) * mm, "end": v(-133.44, 68.5) * mm});
            skArc(sketch, "E81.trimOffspring", {"start": v(-135.7, 69.03) * mm, "mid": v(-137.04, 69.32) * mm, "end": v(-138.38, 69.6) * mm});
            skArc(sketch, "E82.trimOffspring", {"start": v(-140.67, 70.04) * mm, "mid": v(-142.02, 70.28) * mm, "end": v(-143.36, 70.5) * mm});
            skArc(sketch, "E83.trimOffspring", {"start": v(-145.66, 70.86) * mm, "mid": v(-147.02, 71.05) * mm, "end": v(-148.38, 71.22) * mm});
            skArc(sketch, "E84.trimOffspring", {"start": v(-150.69, 71.48) * mm, "mid": v(-152.05, 71.61) * mm, "end": v(-153.41, 71.73) * mm});
            skArc(sketch, "E85.trimOffspring", {"start": v(-155.74, 71.9) * mm, "mid": v(-157.1, 71.97) * mm, "end": v(-158.47, 72.04) * mm});
            skArc(sketch, "E86.trimOffspring", {"start": v(-160.8, 72.11) * mm, "mid": v(-162.16, 72.14) * mm, "end": v(-163.53, 72.15) * mm});
            const initialGuessF0  = {"E2.5.0.0": [-0.16973142002971925, 0.07219369628424277, -0.043445019893348216, 0.9990558193847162, 0.001, 0.0007199110732306023, 6.283185307179576, 0.0033095942654124237], "E2.5.0.3": [-0.16973142002971975, 0.07219369628424324, -0.04344501989332826, 0.999055819384717, 0.001, 0.00075, 4.958959793330974, 0], "E3.1.0": [-0.16466282412411928, 0.07233229395824106, -0.0036916943741007596, 0.9999931856731066, 0.001, 0.00075, 4.958959793330974, 0], "E3.2.0": [-0.15959272530397678, 0.0722692723468923, 0.03606746847274299, 0.9993493571909515, 0.001, 0.00075, 4.958959793330974, 0], "E3.3.0": [-0.1545291404376624, 0.07200473110031833, 0.07576960123842923, 0.9971253519634178, 0.001, 0.00075, 4.958959793330974, 0], "E3.4.0": [-0.14948007609364625, 0.07153908851260518, 0.11535192669046476, 0.993324686599904, 0.001, 0.00075, 4.958959793330974, 0], "E3.5.0": [-0.14445351588046815, 0.07087308086039476, 0.15475185703634523, 0.9879533707335598, 0.001, 0.00075, 4.958959793330974, 0], "E3.6.0": [-0.13945740782301158, 0.07000776123868, 0.1939070928877194, 0.9810198975188187, 0.001, 0.00075, 4.958959793330974, 0], "E3.7.0": [-0.13449965179504192, 0.06894449789564518, 0.23275572176853035, 0.9725352302019761, 0.001, 0.00075, 4.9589597933310285, 6.283185307179581], "E3.8.0": [-0.12958808702788402, 0.0676849720691847, 0.271236316011356, 0.9625127847860452, 0.001, 0.00075, 4.958959793331054, 6.283185307179574], "E3.9.0": [-0.12473047971498397, 0.0662311753285199, 0.3092880298871917, 0.9509684088172958, 0.001, 0.00075, 4.9589597933310205, 6.283185307179583], "E3.10.0": [-0.11993451073196229, 0.06458540642511894, 0.3468506958150451, 0.937920356327028, 0.001, 0.00075, 4.9589597933309975, 0], "E3.11.0": [-0.11520776349157044, 0.06275026765789829, 0.3838649194992511, 0.9233892589681958, 0.001, 0.00075, 4.958959793331053, 6.283185307179583], "E3.12.0": [-0.11055771195275665, 0.06072866075845333, 0.42027217384406174, 0.9073980933925234, 0.001, 0.00075, 4.958959793331085, 0], "E3.13.0": [-0.10599170880280051, 0.058523782302824054, 0.4560148914970145, 0.8899721449196969, 0.001, 0.00075, 4.958959793331079, 6.28318530717958], "E3.14.0": [-0.10151697383120294, 0.05613911865705143, 0.49103655587474887, 0.8711389675560752, 0.001, 0.00075, 4.958959793331048, 0], "E3.15.0": [-0.0971405825137153, 0.053578440464516014, 0.5252817905273417, 0.850928340426143, 0.001, 0.00075, 4.95895979333107, 0], "E3.16.0": [-0.09286945482455754, 0.05084579668377587, 0.5586964466998571, 0.8293722206855941, 0.001, 0.00075, 4.9589597933311005, 0], "E3.17.0": [-0.08871034429451688, 0.04794550818633067, 0.5912276889526574, 0.8065046929904994, 0.001, 0.00075, 4.9589597933311005, 6.283185307179584], "E3.18.0": [-0.08466982733222739, 0.044882160924435824, 0.6228240787050939, 0.78236191560246, 0.001, 0.00075, 4.958959793331101, 0], "E3.19.0": [-0.08075429282551604, 0.04166059867976932, 0.6534356555704757, 0.7569820632149633, 0.001, 0.00075, 4.958959793331106, 6.283185307179582], "E3.20.0": [-0.07696993203925809, 0.03828591540441725, 0.6830140163537097, 0.7304052665913455, 0.001, 0.00075, 4.958959793331145, 0], "E3.21.0": [-0.0733227288257145, 0.0347634471662886, 0.7115123915867018, 0.7026735491098066, 0.001, 0.00075, 4.958959793331147, 6.283185307179584], "E3.22.0": [-0.06981845016283174, 0.031098763711694954, 0.738885719480499, 0.6738307603158121, 0.001, 0.00075, 4.958959793331138, 0], "E3.23.0": [-0.06646263703546418, 0.027297659658436835, 0.7650907171772393, 0.6439225065869476, 0.001, 0.00075, 4.958959793331191, 6.283185307179582], "E3.24.0": [-0.0632605956739381, 0.023366145333321847, 0.7900859491892479, 0.6129960790198625, 0.001, 0.00075, 4.958959793331166, 6.283185307179583], "E3.25.0": [-0.06021738916381096, 0.019310437268602765, 0.8138318929170585, 0.5811003786533249, 0.001, 0.00075, 4.958959793331188, 6.2831853071795845], "E3.26.0": [-0.05733782944009236, 0.015136948372361958, 0.8362910011427683, 0.5482858391456286, 0.001, 0.00075, 4.958959793331165, 6.283185307179584], "E3.27.0": [-0.05462646967858571, 0.010852277788385822, 0.8574277613999063, 0.5146043470286132, 0.001, 0.00075, 4.958959793331168, 6.283185307179584], "E3.28.0": [-0.05208759709638151, 0.006463200461561902, 0.877208752125942, 0.480109159664391, 0.001, 0.00075, 4.9589597933311875, 0], "E3.29.0": [-0.04972522617288575, 0.001976656425298623, 0.8956026955086459, 0.44485482103451196, 0.001, 0.00075, 4.958959793331193, 0], "E3.30.0": [-0.047543092302103, -0.0026002601720942764, 0.9125805069427397, 0.40889707549471677, 0.001, 0.00075, 4.958959793331196, 6.283185307179585], "E3.31.0": [-0.04554464588621052, -0.007260312284712134, 0.9281153410186352, 0.37229277963165325, 0.001, 0.00075, 4.958959793331207, 6.283185307179585], "E3.32.0": [-0.04373304687976326, -0.011996131412312677, 0.9421826339705444, 0.3350998123609249, 0.001, 0.00075, 4.958959793331211, 0], "E3.33.0": [-0.04211115979315627, -0.016800229251429377, 0.9547601425168435, 0.2973769834086302, 0.001, 0.00075, 4.958959793331221, 0], "E3.34.0": [-0.040681549163244964, -0.021665009535918295, 0.9658279790312715, 0.2591839403210967, 0.001, 0.00075, 4.95895979333123, 0], "E3.35.0": [-0.03944647549828499, -0.02658278004821657, 0.9753686429893563, 0.2205810741498498, 0.001, 0.00075, 4.958959793331255, 0], "E3.36.0": [-0.03840789170360448, -0.031545764782319075, 0.9833670486403407, 0.18162942396094758, 0.001, 0.00075, 4.958959793331272, 6.283185307179584], "E3.37.0": [-0.03756743999365883, -0.036546116239242615, 0.9898105488608551, 0.14239058031967125, 0.001, 0.00075, 4.958959793331263, 0], "E3.38.0": [-0.036926449295352534, -0.04157592783553454, 0.9946889551526189, 0.10292658790318124, 0.001, 0.00075, 4.958959793331271, 6.283185307179585], "E3.39.0": [-0.03648593314673225, -0.04662724640520646, 0.9979945537525511, 0.06329984739513, 0.001, 0.00075, 4.958959793331281, 6.2831853071795845], "E3.40.0": [-0.03624658809437499, -0.0516920847753245, 0.9997221178298141, 0.023573016817354835, 0.001, 0.00075, 4.958959793331237, 6.283185307179583], "E3.41.0": [-0.03620879259200492, -0.056762434395371264, 0.9998689157505095, -0.016191087545333643, 0.001, 0.00075, 4.958959793331282, 0], "E3.42.0": [-0.03637260640207987, -0.061830278000410466, 0.9984347153969508, -0.055929590470609455, 0.001, 0.00075, 4.958959793331263, 0], "E3.43.0": [-0.03673777050129497, -0.06688760228803056, 0.9954217845346902, -0.09557965721728141, 0.001, 0.00075, 4.958959793331296, 0], "E3.44.0": [-0.03730370749015158, -0.07192641058902316, 0.990834887226715, -0.13507859287993426, 0.001, 0.00075, 4.958959793331342, 6.283185307179583], "E3.45.0": [-0.03806952250594456, -0.07693873551176053, 0.9846812763004849, -0.17436394152246107, 0.001, 0.00075, 4.958959793331377, 6.283185307179577], "E3.46.0": [-0.03903400463772411, -0.08191665154027944, 0.9769706818797206, -0.21337358493373546, 0.001, 0.00075, 4.958959793331333, 0], "E3.47.0": [-0.04019562884099512, -0.08685228756615115, 0.9677152959990782, -0.25204584084927145, 0.001, 0.00075, 4.958959793331307, 0], "E3.48.0": [-0.04155255834912577, -0.09173783933432147, 0.9569297533260375, -0.2903195604835626, 0.001, 0.00075, 4.958959793331397, 0], "E3.49.0": [-0.043102647577652975, -0.09656558178324229, 0.9446311080204829, -0.32813422521888, 0.001, 0.00075, 4.9589597933314185, 0], "E3.50.0": [-0.04484344551689273, -0.10132788125978162, 0.9308388067685726, -0.36543004229764703, 0.001, 0.00075, 4.958959793331372, 6.283185307179581], "E3.51.0": [-0.046772199607490184, -0.1060172075895982, 0.9155746580335294, -0.40214803936707894, 0.001, 0.00075, 4.9589597933314105, 6.283185307179582], "E3.52.0": [-0.04888586009278145, -0.11062614598389531, 0.8988627975719797, -0.43823015772659285, 0.001, 0.00075, 4.958959793331331, 0], "E3.53.0": [-0.051181084841086244, -0.1151474087637254, 0.8807296502703585, -0.47361934413054957, 0.001, 0.00075, 4.958959793331408, 6.283185307179581], "E3.54.0": [-0.05365424463030455, -0.11957384688330891, 0.8612038883617348, -0.5082596410011605, 0.001, 0.00075, 4.958959793331408, 6.283185307179581], "E3.55.0": [-0.056301428886462945, -0.12389846123414468, 0.8403163860891167, -0.5420962749089193, 0.001, 0.00075, 4.958959793331378, 0], "E3.56.0": [-0.05911845186713602, -0.12811441371203952, 0.8181001708869273, -0.5750757431806529, 0.001, 0.00075, 4.9589597933314415, 6.283185307179572], "E3.57.0": [-0.06210085927996514, -0.13221503802955625, 0.7945903711578418, -0.6071458984982465, 0.001, 0.00075, 4.958959793331429, 6.283185307179584], "E3.58.0": [-0.06524393532581058, -0.13619385025678446, 0.7698241607275628, -0.6382560313542706, 0.001, 0.00075, 4.958959793331431, 6.2831853071795685], "E3.59.0": [-0.068542710155399, -0.14004455907376634, 0.7438407000653613, -0.6683569502341344, 0.001, 0.00075, 4.958959793331498, 0], "E3.60.0": [-0.0719919677276768, -0.14376107571836674, 0.7166810743633254, -0.6974010593979836, 0.001, 0.00075, 4.958959793331474, 0], "E3.61.0": [-0.07558625405744321, -0.14733752361385766, 0.6883882285722254, -0.7253424341393475, 0.001, 0.00075, 4.958959793331471, 6.2831853071795845], "E3.62.0": [-0.07931988583922192, -0.15076824766099406, 0.6590068994967213, -0.752136893401539, 0.001, 0.00075, 4.958959793331465, 0], "E3.63.0": [-0.08318695943373519, -0.15404782317988774, 0.6285835450572784, -0.7777420696369872, 0.001, 0.00075, 4.95895979333149, 0], "E3.64.0": [-0.08718136020277067, -0.1571710644875417, 0.5971662708306466, -0.802117475799037, 0.001, 0.00075, 4.958959793331485, 0], "E3.65.0": [-0.09129677217768203, -0.16013303309748073, 0.5648047539850536, -0.8252245693602943, 0.001, 0.00075, 4.958959793331503, 0], "E3.66.0": [-0.09552668804623293, -0.16292904552851342, 0.531550164730393, -0.8470268132562817, 0.001, 0.00075, 4.958959793331519, 0], "E3.67.0": [-0.09986441944199537, -0.16555468071027887, 0.49745508540760425, -0.8674897336580492, 0.001, 0.00075, 4.958959793331513, 0], "E3.68.0": [-0.10430310752003197, -0.16800578697386753, 0.4625734273451838, -0.8865809744823818, 0.001, 0.00075, 4.958959793331488, 6.283185307179583], "E3.69.0": [-0.10883573380213946, -0.17027848861646297, 0.42696034561429236, -0.9042703485534204, 0.001, 0.00075, 4.958959793331494, 6.2831853071795845], "E3.70.0": [-0.1134551312745054, -0.17236919202962492, 0.3906721518172509, -0.9205298853347885, 0.001, 0.00075, 4.958959793331546, 0], "E3.71.0": [-0.11815399572023014, -0.1742745913815228, 0.3537662250473238, -0.9353338751567625, 0.001, 0.00075, 4.958959793330931, 6.283185307179581], "E3.72.0": [-0.12292489726879477, -0.175991673844135, 0.31630092116057856, -0.9486589098685415, 0.001, 0.00075, 4.95895979333151, 0], "E3.73.0": [-0.12776029214421447, -0.17751772435714985, 0.2783354805032802, -0.9604839198513467, 0.001, 0.00075, 4.958959793330996, 6.283185307179569], "E3.74.0": [-0.1326525345932979, -0.17885032992103367, 0.23992993424072911, -0.970790207333819, 0.001, 0.00075, 4.958959793330997, 0], "E3.75.0": [-0.1375938889751552, -0.17998738341247894, 0.20114500943565006, -0.9795614759570388, 0.001, 0.00075, 4.958959793330994, 0], "E3.76.0": [-0.14257654199283587, -0.1809270869161996, 0.16204203302622294, -0.9867838565424187, 0.001, 0.00075, 4.958959793330983, 0], "E3.77.0": [-0.14759261504775772, -0.18166795456780457, 0.12268283485558747, -0.992445929021726, 0.001, 0.00075, 4.958959793330972, 6.2831853071795845], "E3.78.0": [-0.15263417669739024, -0.18220881490325466, 0.08312964990615296, -0.9965387404945584, 0.001, 0.00075, 4.958959793330969, 6.283185307179576], "E4.1.1": [-0.1646628241241188, 0.07233229395824056, -0.0036916943741207298, 0.9999931856731066, 0.001, 0.0007199110732306023, 6.283185307179576, 1.3242255138486365], "E4.2.1": [-0.15959272530397633, 0.07226927234689179, 0.03606746847272302, 0.9993493571909522, 0.001, 0.0007199110732306023, 6.283185307179576, 1.3242255138486365], "E4.3.1": [-0.15452914043766194, 0.07200473110031781, 0.07576960123840928, 0.9971253519634191, 0.001, 0.0007199110732306023, 6.283185307179576, 1.3242255138486365], "E4.4.1": [-0.1494800760936458, 0.07153908851260463, 0.11535192669044494, 0.9933246865999065, 0.001, 0.0007199110732306023, 6.283185307179576, 1.3242255138486365], "E4.5.1": [-0.14445351588046776, 0.0708730808603942, 0.1547518570363255, 0.9879533707335629, 0.001, 0.0007199110732306023, 6.283185307179576, 1.3242255138486365], "E4.6.1": [-0.13945740782301122, 0.07000776123867941, 0.1939070928876998, 0.9810198975188226, 0.001, 0.0007199110732306023, 6.283185307179576, 1.3242255138486365], "E4.7.1": [-0.1344996517950419, 0.06894449789564466, 0.23275572176850848, 0.9725352302019813, 0.001, 0.0007199110732306023, 6.283185307179576, 1.3242255138486365], "E4.8.1": [-0.1295880870278841, 0.0676849720691842, 0.2712363160113341, 0.9625127847860515, 0.001, 0.0007199110732306023, 6.283185307179576, 1.3242255138486365], "E4.9.1": [-0.12473047971498408, 0.06623117532851938, 0.3092880298871697, 0.9509684088173033, 0.001, 0.0007199110732306023, 6.283185307179576, 1.3242255138486365], "E4.10.1": [-0.11993451073196246, 0.06458540642511842, 0.346850695815023, 0.9379203563270362, 0.001, 0.0007199110732306023, 6.283185307179576, 1.3242255138486365], "E4.11.1": [-0.11520776349157066, 0.06275026765789786, 0.38386491949922896, 0.9233892589682049, 0.001, 0.0007199110732306023, 6.283185307179576, 1.3242255138486365], "E4.12.1": [-0.11055771195275693, 0.06072866075845293, 0.42027217384403986, 0.9073980933925337, 0.001, 0.0007199110732306023, 6.283185307179576, 1.3242255138486365], "E4.13.1": [-0.10599170880280084, 0.05852378230282365, 0.4560148914969927, 0.8899721449197081, 0.001, 0.0007199110732306023, 6.283185307179576, 1.3242255138486365], "E4.14.1": [-0.10151697383120334, 0.05613911865705104, 0.49103655587472705, 0.8711389675560876, 0.001, 0.0007199110732306023, 6.283185307179576, 1.3242255138486365], "E4.15.1": [-0.09714058251371577, 0.053578440464515695, 0.5252817905273202, 0.8509283404261565, 0.001, 0.0007199110732306023, 6.283185307179576, 1.3242255138486365], "E4.16.1": [-0.09286945482455802, 0.050845796683775576, 0.5586964466998359, 0.8293722206856085, 0.001, 0.0007199110732306023, 6.283185307179576, 1.3242255138486365], "E4.17.1": [-0.08871034429451743, 0.04794550818633042, 0.5912276889526366, 0.8065046929905149, 0.001, 0.0007199110732306023, 6.283185307179576, 1.3242255138486365], "E4.18.1": [-0.08466982733222776, 0.04488216092443546, 0.6228240787050753, 0.782361915602475, 0.001, 0.0007199110732306023, 6.283185307179585, 1.3242255138487098], "E4.19.1": [-0.08075429282551644, 0.041660598679768956, 0.6534356555704576, 0.7569820632149791, 0.001, 0.0007199110732306023, 0, 1.3242255138486823], "E4.20.1": [-0.0769699320392585, 0.038285915404416976, 0.6830140163536919, 0.7304052665913621, 0.001, 0.0007199110732306023, 0, 1.324225513848732], "E4.21.1": [-0.07332272882571494, 0.034763447166288375, 0.7115123915866846, 0.7026735491098243, 0.001, 0.0007199110732306023, 6.283185307179584, 1.3242255138487655], "E4.22.1": [-0.06981845016283222, 0.031098763711694732, 0.7388857194804823, 0.6738307603158304, 0.001, 0.0007199110732306023, 6.283185307179585, 1.324225513848715], "E4.23.1": [-0.0664626370354647, 0.027297659658436668, 0.7650907171772231, 0.6439225065869668, 0.001, 0.0007199110732306023, 6.283185307179582, 1.3242255138487005], "E4.24.1": [-0.06326059567393866, 0.023366145333321736, 0.7900859491892324, 0.6129960790198824, 0.001, 0.0007199110732306023, 0, 1.3242255138487373], "E4.25.1": [-0.06021738916381153, 0.01931043726860271, 0.8138318929170437, 0.5811003786533456, 0.001, 0.0007199110732306023, 6.283185307179584, 1.3242255138487105], "E4.26.1": [-0.05733782944009294, 0.01513694837236193, 0.8362910011427542, 0.5482858391456502, 0.001, 0.0007199110732306023, 0, 1.3242255138487347], "E4.27.1": [-0.054626469678586316, 0.010852277788385822, 0.857427761399893, 0.5146043470286356, 0.001, 0.0007199110732306023, 0, 1.3242255138487424], "E4.28.1": [-0.05208759709638212, 0.006463200461561958, 0.8772087521259293, 0.48010915966441403, 0.001, 0.0007199110732306023, 0, 1.3242255138487553], "E4.29.1": [-0.049725226172886425, 0.0019766564252986785, 0.8956026955086343, 0.44485482103453566, 0.001, 0.0007199110732306023, 0, 1.3242255138486887], "E4.30.1": [-0.04754309230210364, -0.0026002601720941376, 0.912580506942729, 0.4088970754947412, 0.001, 0.0007199110732306023, 0, 1.3242255138487482], "E4.31.1": [-0.04554464588621115, -0.007260312284711967, 0.9281153410186251, 0.3722927796316781, 0.001, 0.0007199110732306023, 0, 1.3242255138487513], "E4.32.1": [-0.04373304687976393, -0.011996131412312427, 0.9421826339705355, 0.3350998123609504, 0.001, 0.0007199110732306023, 0, 1.3242255138487395], "E4.33.1": [-0.04211115979315693, -0.016800229251429044, 0.9547601425168354, 0.2973769834086563, 0.001, 0.0007199110732306023, 6.283185307179584, 1.3242255138487493], "E4.34.1": [-0.04068154916324559, -0.021665009535917934, 0.9658279790312644, 0.25918394032112335, 0.001, 0.0007199110732306023, 6.283185307179584, 1.3242255138487549], "E4.35.1": [-0.03944647549828564, -0.026582780048216154, 0.9753686429893503, 0.22058107414987685, 0.001, 0.0007199110732306023, 0, 1.3242255138487402], "E4.36.1": [-0.038407891703605083, -0.03154576478231863, 0.9833670486403358, 0.1816294239609751, 0.001, 0.0007199110732306023, 6.2831853071795845, 1.3242255138487589], "E4.37.1": [-0.03756743999365947, -0.036546116239242116, 0.9898105488608511, 0.14239058031969914, 0.001, 0.0007199110732306023, 0, 1.3242255138487495], "E4.38.1": [-0.03692644929535313, -0.04157592783553396, 0.994688955152616, 0.10292658790320952, 0.001, 0.0007199110732306023, 6.2831853071795845, 1.3242255138487613], "E4.39.1": [-0.036485933146732805, -0.04662724640520585, 0.9979945537525492, 0.06329984739515858, 0.001, 0.0007199110732306023, 6.283185307179584, 1.3242255138487937], "E4.40.1": [-0.03624658809437556, -0.05169208477532383, 0.9997221178298135, 0.023573016817383684, 0.001, 0.0007199110732306022, 0, 1.324225513848807], "E4.41.1": [-0.036208792592005434, -0.05676243439537057, 0.9998689157505098, -0.016191087545304576, 0.001, 0.0007199110732306023, 0, 1.3242255138487826], "E4.42.1": [-0.036372606402080385, -0.061830278000409716, 0.9984347153969523, -0.0559295904705802, 0.001, 0.0007199110732306023, 0, 1.3242255138487808], "E4.43.1": [-0.036737770501295425, -0.06688760228802976, 0.9954217845346929, -0.09557965721725198, 0.001, 0.0007199110732306023, 0, 1.3242255138487908], "E4.44.1": [-0.03730370749015198, -0.0719264105890223, 0.9908348872267191, -0.1350785928799048, 0.001, 0.0007199110732306023, 6.283185307179581, 1.3242255138488013], "E4.45.1": [-0.038069522505944905, -0.07693873551175962, 0.9846812763004902, -0.1743639415224316, 0.001, 0.0007199110732306023, 0, 1.3242255138487715], "E4.46.1": [-0.039034004637724454, -0.0819166515402785, 0.976970681879727, -0.21337358493370595, 0.001, 0.0007199110732306023, 0, 1.3242255138487735], "E4.47.1": [-0.04019562884099545, -0.08685228756615015, 0.9677152959990861, -0.252045840849242, 0.001, 0.0007199110732306023, 6.2831853071795845, 1.324225513848782], "E4.48.1": [-0.04155255834912601, -0.09173783933432045, 0.9569297533260466, -0.2903195604835332, 0.001, 0.0007199110732306023, 0, 1.3242255138487662], "E4.49.1": [-0.04310264757765317, -0.09656558178324123, 0.9446311080204931, -0.3281342252188509, 0.001, 0.0007199110732306023, 0, 1.3242255138487833], "E4.50.1": [-0.0448434455168929, -0.10132788125978048, 0.930838806768584, -0.3654300422976181, 0.001, 0.0007199110732306023, 6.28318530717958, 1.324225513848785], "E4.51.1": [-0.04677219960749024, -0.10601720758959711, 0.9155746580335422, -0.40214803936705007, 0.001, 0.0007199110732306023, 6.283185307179577, 1.3242255138488224], "E4.52.1": [-0.04888586009278151, -0.11062614598389417, 0.8988627975719935, -0.43823015772656443, 0.001, 0.0007199110732306023, 6.283185307179585, 1.3242255138488324], "E4.53.1": [-0.051181084841086216, -0.11514740876372426, 0.8807296502703736, -0.47361934413052176, 0.001, 0.0007199110732306023, 6.2831853071795845, 1.3242255138488317], "E4.54.1": [-0.05365424463030444, -0.1195738468833077, 0.8612038883617512, -0.508259641001133, 0.001, 0.0007199110732306023, 6.283185307179579, 1.3242255138488377], "E4.55.1": [-0.056301428886462807, -0.12389846123414348, 0.8403163860891343, -0.5420962749088921, 0.001, 0.0007199110732306022, 6.2831853071795845, 1.3242255138488594], "E4.56.1": [-0.05911845186713585, -0.12811441371203824, 0.818100170886946, -0.5750757431806266, 0.001, 0.0007199110732306023, 6.283185307179575, 1.3242255138487706], "E4.57.1": [-0.06210085927996484, -0.132215038029555, 0.7945903711578617, -0.6071458984982209, 0.001, 0.0007199110732306023, 6.283185307179581, 1.3242255138488714], "E4.58.1": [-0.06524393532581022, -0.1361938502567832, 0.7698241607275839, -0.6382560313542452, 0.001, 0.0007199110732306023, 6.2831853071795765, 1.324225513848871], "E4.59.1": [-0.06854271015539853, -0.14004455907376506, 0.7438407000653835, -0.6683569502341097, 0.001, 0.0007199110732306023, 6.283185307179579, 1.3242255138488268], "E4.60.1": [-0.07199196772767627, -0.14376107571836547, 0.7166810743633486, -0.6974010593979597, 0.001, 0.0007199110732306023, 6.28318530717957, 1.3242255138488546], "E4.61.1": [-0.07558625405744268, -0.14733752361385646, 0.6883882285722497, -0.7253424341393245, 0.001, 0.0007199110732306023, 0, 1.3242255138488273], "E4.62.1": [-0.07931988583922134, -0.1507682476609928, 0.6590068994967466, -0.752136893401517, 0.001, 0.0007199110732306023, 0, 1.3242255138488337], "E4.63.1": [-0.0831869594337345, -0.1540478231798865, 0.6285835450573051, -0.7777420696369658, 0.001, 0.0007199110732306023, 0, 1.324225513848872], "E4.64.1": [-0.08718136020276993, -0.15717106448754045, 0.597166270830674, -0.8021174757990167, 0.001, 0.0007199110732306023, 6.283185307179575, 1.3242255138488364], "E4.65.1": [-0.09129677217768126, -0.16013303309747948, 0.5648047539850819, -0.825224569360275, 0.001, 0.0007199110732306023, 0, 1.324225513848812], "E4.66.1": [-0.09552668804623202, -0.16292904552851223, 0.5315501647304224, -0.8470268132562635, 0.001, 0.0007199110732306023, 0, 1.3242255138488381], "E4.67.1": [-0.09986441944199442, -0.16555468071027768, 0.4974550854076347, -0.8674897336580317, 0.001, 0.0007199110732306023, 0, 1.324225513848834], "E4.68.1": [-0.10430310752003094, -0.16800578697386637, 0.46257342734521506, -0.8865809744823657, 0.001, 0.0007199110732306023, 0, 1.3242255138488674], "E4.69.1": [-0.10883573380213835, -0.17027848861646183, 0.4269603456143241, -0.9042703485534053, 0.001, 0.0007199110732306023, 0, 1.3242255138488728], "E4.70.1": [-0.11345513127450424, -0.17236919202962384, 0.3906721518172835, -0.9205298853347748, 0.001, 0.0007199110732306023, 0, 1.3242255138488648], "E4.71.1": [-0.11815399572022886, -0.17427459138152168, 0.3537662250473576, -0.9353338751567498, 0.001, 0.0007199110732306023, 6.2831853071795845, 1.3242255138488883], "E4.72.1": [-0.12292489726879346, -0.17599167384413397, 0.31630092116061265, -0.9486589098685302, 0.001, 0.0007199110732306023, 6.283185307179584, 1.3242255138489107], "E4.73.1": [-0.12776029214421303, -0.17751772435714888, 0.2783354805033148, -0.9604839198513367, 0.001, 0.0007199110732306023, 0, 1.3242255138488406], "E4.74.1": [-0.13265253459329648, -0.17885032992103272, 0.23992993424076448, -0.9707902073338104, 0.001, 0.0007199110732306023, 0, 1.324225513848858], "E4.75.1": [-0.13759388897515362, -0.17998738341247808, 0.20114500943568614, -0.9795614759570315, 0.001, 0.0007199110732306023, 0, 1.3242255138488843], "E4.76.1": [-0.1425765419928343, -0.1809270869161988, 0.16204203302625925, -0.9867838565424126, 0.001, 0.0007199110732306023, 6.283185307179573, 1.3242255138488968], "E4.77.1": [-0.14759261504775614, -0.18166795456780382, 0.12268283485562403, -0.9924459290217215, 0.001, 0.0007199110732306023, 6.283185307179571, 1.324225513848928], "E4.78.1": [-0.1526341766973885, -0.18220881490325394, 0.08312964990619012, -0.9965387404945552, 0.001, 0.0007199110732306023, 0, 1.3242255138488832], "E4.79.1": [-0.1576932551964936, -0.18254881271118756, 0.04344501989333769, -0.9990558193847167, 0.001, 0.0007199110732306023, 0, 1.3242255138488794]};
            skSetInitialGuess(sketch, initialGuessF0);
            skSolve(sketch);
        }
        {
            var Q0;
            Q0=qSketchRegion(id+"F0",true);
            extrude(context, id + "F1", {"entities" : qUnion([Q0]), "depth" : 10 * mm, "offsetDistance" : 25 * mm});
        }
    });
